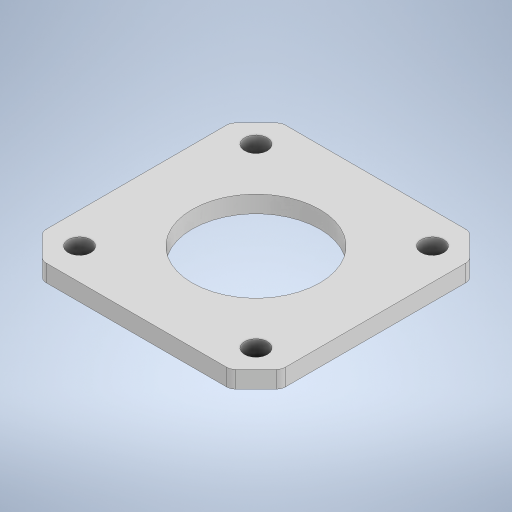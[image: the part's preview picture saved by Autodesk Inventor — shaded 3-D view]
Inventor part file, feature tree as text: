
AUTODESK INVENTOR PART (.ipt)
format: ipt  version: 2024 (Build 280153000, 153)  size: 419,840 bytes
history: native  units: mm
features: other x3, plane x1, extrude x1, sketch x1, reference x1
ambient origin geometry x8: Origin, YZ Plane, XZ Plane, XY Plane, X Axis, Y Axis, Z Axis, Center Point
bodies: Solid1 (feature_tree)
feature tree (7):
  plane  "Work Plane1"
  extrude  "Extrusion1"  Depth=3.0mm
  sketch  "Sketch1"  dims[d0=4.0mm d1=4.0mm d2=4.0mm d3=4.0mm d4=3.0mm d5=0.0mm]
  reference  "Reference1"
  other  "<userpath> windows\Documents\Inventor\Robotska_roka\roka.iam"
  other  "roka.iam"
  other  "Nema 17 Motor a Pasos 17HS4401:3"
